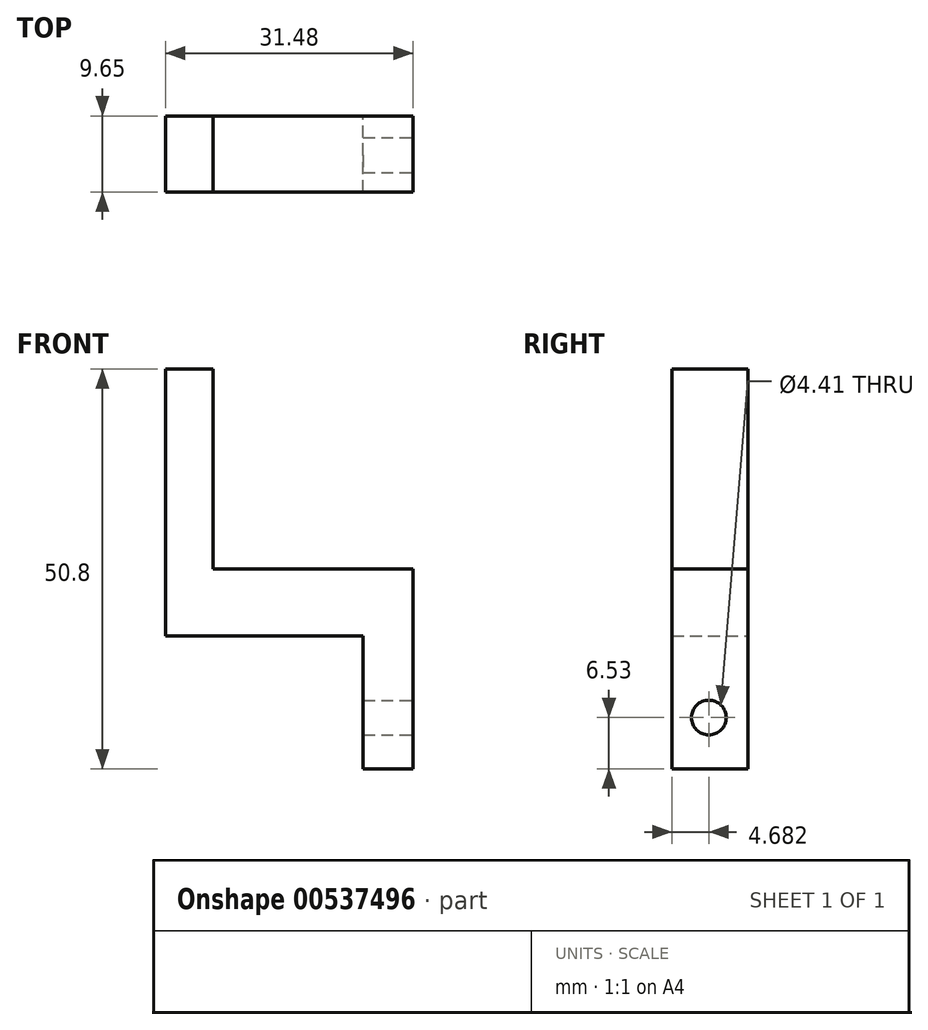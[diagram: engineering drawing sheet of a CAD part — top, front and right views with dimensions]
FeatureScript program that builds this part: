
annotation { "Feature Type Name" : "Feature", "Feature Type Description" : "" }
export const myFeature = defineFeature(function(context is Context, id is Id, definition is map)
    precondition{}
    {
        {
            var Q0;
            Q0=qCreatedBy(makeId("Front.planeOp"),FACE);
            var sketch = newSketch(context, id + "F0", { "sketchPlane" : qUnion([Q0])});
            skLineSegment(sketch, "E0", {"start": v(-44.8, 40.7) * mm, "end": v(-44.8, 15.3) * mm});
            skLineSegment(sketch, "E1", {"start": v(-44.8, 15.3) * mm, "end": v(-19.4, 15.3) * mm});
            skLineSegment(sketch, "E2", {"start": v(-19.4, 15.3) * mm, "end": v(-19.4, -10.1) * mm});
            skLineSegment(sketch, "E3", {"start": v(-19.4, -10.1) * mm, "end": v(-25.75, -10.1) * mm});
            skLineSegment(sketch, "E4", {"start": v(-25.75, -10.1) * mm, "end": v(-25.75, 6.82) * mm});
            skLineSegment(sketch, "E5", {"start": v(-25.75, 6.82) * mm, "end": v(-50.88, 6.82) * mm});
            skLineSegment(sketch, "E6", {"start": v(-50.88, 6.82) * mm, "end": v(-50.88, 40.7) * mm});
            skLineSegment(sketch, "E7", {"start": v(-44.8, 40.7) * mm, "end": v(-50.88, 40.7) * mm});
            skSolve(sketch);
        }
        {
            var Q0;
            Q0 = qSketchRegion(id + "F0", true);
            extrude(context, id + "F1", {"entities" : qUnion([Q0]), "depth" : 9.65 * mm, "offsetDistance" : 25.4 * mm});
        }
        {
            var Q0;
            Q0=makeQuery(id+"F1.opExtrude","SWEPT_FACE",FACE,{"disambiguationData":[OSD([sQuery(id+"F0.wireOp",EDGE,"E2")])]});
            var sketch = newSketch(context, id + "F2", { "sketchPlane" : qUnion([Q0])});
            skCircle(sketch, "E8", {"center": v(-4.97, -3.57) * mm, "radius": 2.2 * mm});
            skSolve(sketch);
        }
        {
            var Q0;
            Q0 = qSketchRegion(id + "F2", true);
            extrude(context, id + "F3", {"entities" : qUnion([Q0]), "operationType" : NewBodyOperationType.REMOVE, "oppositeDirection" : true, "depth" : 25.4 * mm, "offsetDistance" : 25.4 * mm});
        }
    });
